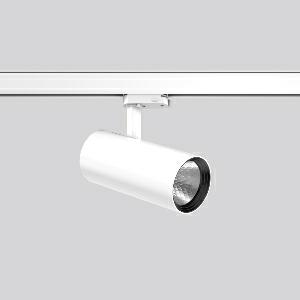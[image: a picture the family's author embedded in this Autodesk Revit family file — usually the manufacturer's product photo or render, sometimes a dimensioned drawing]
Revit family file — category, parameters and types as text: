
# Revit family: deecos_s_mini_742196_002_52e3
name_source: partatom
category: Lighting Fixtures
units: mm (PartAtom-declared; Revit-internal decimal feet)

## family parameters
Cut with Voids When Loaded = No
Host = Face
Light Source = No
Part Type = Normal
Room Calculation Point = No
Round Connector Dimension = Use Diameter
Shared = No

## types (1)
- DEECOS S mini (1 x LED Modul 930, 2450 lm, 3000)
    Apparent Load = 20 VA
    Approval mark = CE
    CIE Flux Codes = 99 100 100 100 100
    Color Rendering = 90
    Color Temperature = 3000
    Default Elevation = 1800 mm
    Description = Series: DEECOS S mini
LED surface-mounted projector in modern design with no visible cooling ribs. Housing: die-cast aluminium, powder-coated. Rotation range: 356°. Swivel range: 90°. Black plastic ring and recessed LED to prevent glare from the side. Optical assembly with reflector made of MIRO-Silver with 98% total light reflection for outstanding efficiency - can be changed without tools. Best colour rendering index Ra>90. With multi adaptor for 3-circuit tracks 230 V. Suitable for Track on ceiling, Wall track. High quality converter without flickering and stroboscopic effect. The following accessories can be mounted without use of tools: interchangeable lenses, decorative glasses, honeycomb louvre, clear and frosted diffusers, white interchangeable plastic ring. 
Colour: traffic white, matt (RAL 9016)
Diameter: 87 mm
Height: 214 mm
Lamp: LED
Socket: without socket
Colour temperature: 3000K
Colour rendering index (CRI): 92
System power: 20 W
Rated luminous flux: 2450 lm
Luminous efficiency: 123 lm/W
Control gear: Regulated power supply
Protection class: I
Type of protection: IP 20
    Height = 214 mm
    Lamp = 1 x LED Modul 930
    Lamp Light Flux = 2450 lm
    Lamp count = 1
    Length = 87 mm
    Lifetime = 50000 h
    Luminous efficacy = 123 lm/W
    Manufacturer = RZB
    ModVariant = No
    Model = 742196.002
    Mounting Place = Ceiling
    Mounting Type = Rail mounted
    Number of Poles = 1
    OnlyDefault = Yes
    Power Factor = 1
    Product Name = DEECOS S mini
    Product group = Track mounted projectors
    ProductGroupID = 301
    Protection Class = Protection class I
    Protection Degree = IP 20
    RLX_Detail_Level = 1
    RLX_Emergency_Light_Flux = 0 lm
    RLX_Emergency_Type = 0
    RLX_Emergency_Type_DB = No
    RlxData = <blob elided: 35505 chars, md5=1e721e22>
    Socket = socket
    Standby Power = 0 W
    System Light Flux = 2450 lm
    System Power = 20 W
    Type Comments = Product without accessories
    Type Image = 741926.002.jpg
    URL = http://relux.com
    VarID = ---
    Voltage = 230 V
    Voltage Range = 220-240 V
    Weight = 0.00 kg
    Width = 0 mm  [stored 0 ft]

note: [stored X ft] marks values corroborated as IEEE doubles in the binary element streams (Revit-internal decimal feet)

## geometry (parser evidence)
native form markers: Blend x4, Sweep x14
no freeform markers — native parametric forms only
